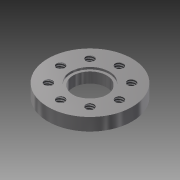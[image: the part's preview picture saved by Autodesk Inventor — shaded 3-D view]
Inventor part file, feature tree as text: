
AUTODESK INVENTOR PART (.ipt)
format: ipt  version: 2013 (Build 170138000, 138)  size: 133,120 bytes
history: native  units: mm
features: sketch x4, extrude x2, hole x2, other x1, pattern_circular x1
ambient origin geometry x1: Origin
feature tree (10):
  other  "ソリッド1"
  extrude  "押し出し1"  Depth=20.0mm
  hole  "穴4"  [1 undecoded]
  hole  "穴5"  [1 undecoded]
  extrude  "押し出し4"  Depth=2.0mm
  pattern_circular  "円形状パターン3"  [2 undecoded]
  sketch  "スケッチ1"
  sketch  "スケッチ2"
  sketch  "スケッチ5"
  sketch  "スケッチ6"
note: 4 required parameter values undecoded (feature->parameter linkage not recoverable at this tier; creation-order binding heuristic only, values carry confidence <= 0.55)
